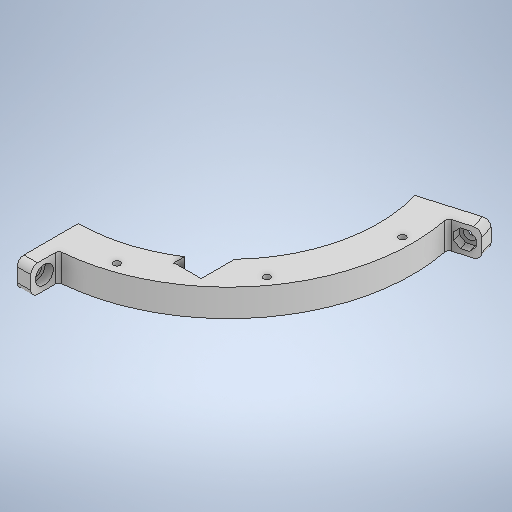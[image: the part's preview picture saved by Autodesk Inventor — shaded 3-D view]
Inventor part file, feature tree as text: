
AUTODESK INVENTOR PART (.ipt)
format: ipt  version: 2025 (Build 290162000, 162)  size: 383,488 bytes
history: native  units: in
note: dims shown in document units (in); Inventor stores cm internally (conversion verified against a paired STEP export)
features: sketch x12, extrude x8, hole x3, fillet x1
ambient origin geometry x8: Origin, YZ Plane, XZ Plane, XY Plane, X Axis, Y Axis, Z Axis, Center Point
bodies: Solid1 (feature_tree)
feature tree (24):
  extrude  "Extrusion1"  Depth=8.6614in
  extrude  "Extrusion2"  Depth=1.4173in
  hole  "Hole1"  [1 undecoded]
  extrude  "Extrusion3"  Depth=0.1575in TaperAngle=360.0deg
  extrude  "Extrusion7"  Depth=0.1575in TaperAngle=0.0deg
  extrude  "Extrusion8"  Depth=2.7559in
  extrude  "Extrusion9"  Depth=0.7874in
  extrude  "Extrusion10"  TaperAngle=0.0deg  [1 undecoded]
  fillet  "Fillet1"  Radius=0.8858in
  hole  "Hole2"  [1 undecoded]
  extrude  "Extrusion11"  Depth=0.3937in TaperAngle=0.0deg
  hole  "Hole3"  [1 undecoded]
  sketch  "Sketch1"  dims[d0=10.6299in d1=8.6614in]
  sketch  "Sketch2"  dims[d5=0.0in d6=0.0in d7=10.0394in]
  sketch  "Sketch3"  dims[d8=0.1575in d9=3.937in d11=360.0deg]
  sketch  "Sketch Circular Pattern1"  dims[d2=1.8504in d3=0.0in d4=1.4173in]
  sketch  "Sketch4"  dims[d13=0.1969in d14=0.3937in d15=0.1575in d16=0.0787in d17=90.0deg d18=0.5591in d19=0.8108in d20=1.063in d21=0.0in]
  sketch  "Sketch7"  dims[d38=0.1181in d39=2.7559in]
  sketch  "Sketch8"  dims[d40=0.7874in d41=7.874in]
  sketch  "Sketch9"  dims[d42=0.5906in d43=0.0in d44=0.0in d45=0.0in d46=0.8858in]
  sketch  "Sketch10"  dims[d47=0.7874in d48=0.7874in]
  sketch  "Sketch11"  dims[d49=0.1969in d50=0.3937in d51=0.0in]
  sketch  "Sketch12"  dims[d52=0.8858in d53=0.7874in]
  sketch  "Sketch13"  dims[d54=0.7874in d55=0.1969in d56=0.3937in d57=0.0in d58=0.0984in d59=0.3937in d60=0.3937in d61=0.3228in d62=0.2362in d63=0.5197in d64=0.2362in d65=90.0deg d66=0.315in d67=0.8108in d68=0.3937in d69=0.3937in d70=0.5197in d71=0.2362in d72=0.0in d73=0.3937in d74=0.3937in d75=0.3228in d76=0.2362in d77=0.5197in d78=0.2362in d79=90.0deg d80=0.315in d81=0.8108in d30=0.0197in d31=0.0344in d32=0.0197in d33=0.0344in]
note: 4 required parameter values undecoded (feature->parameter linkage not recoverable at this tier; creation-order binding heuristic only, values carry confidence <= 0.55)
